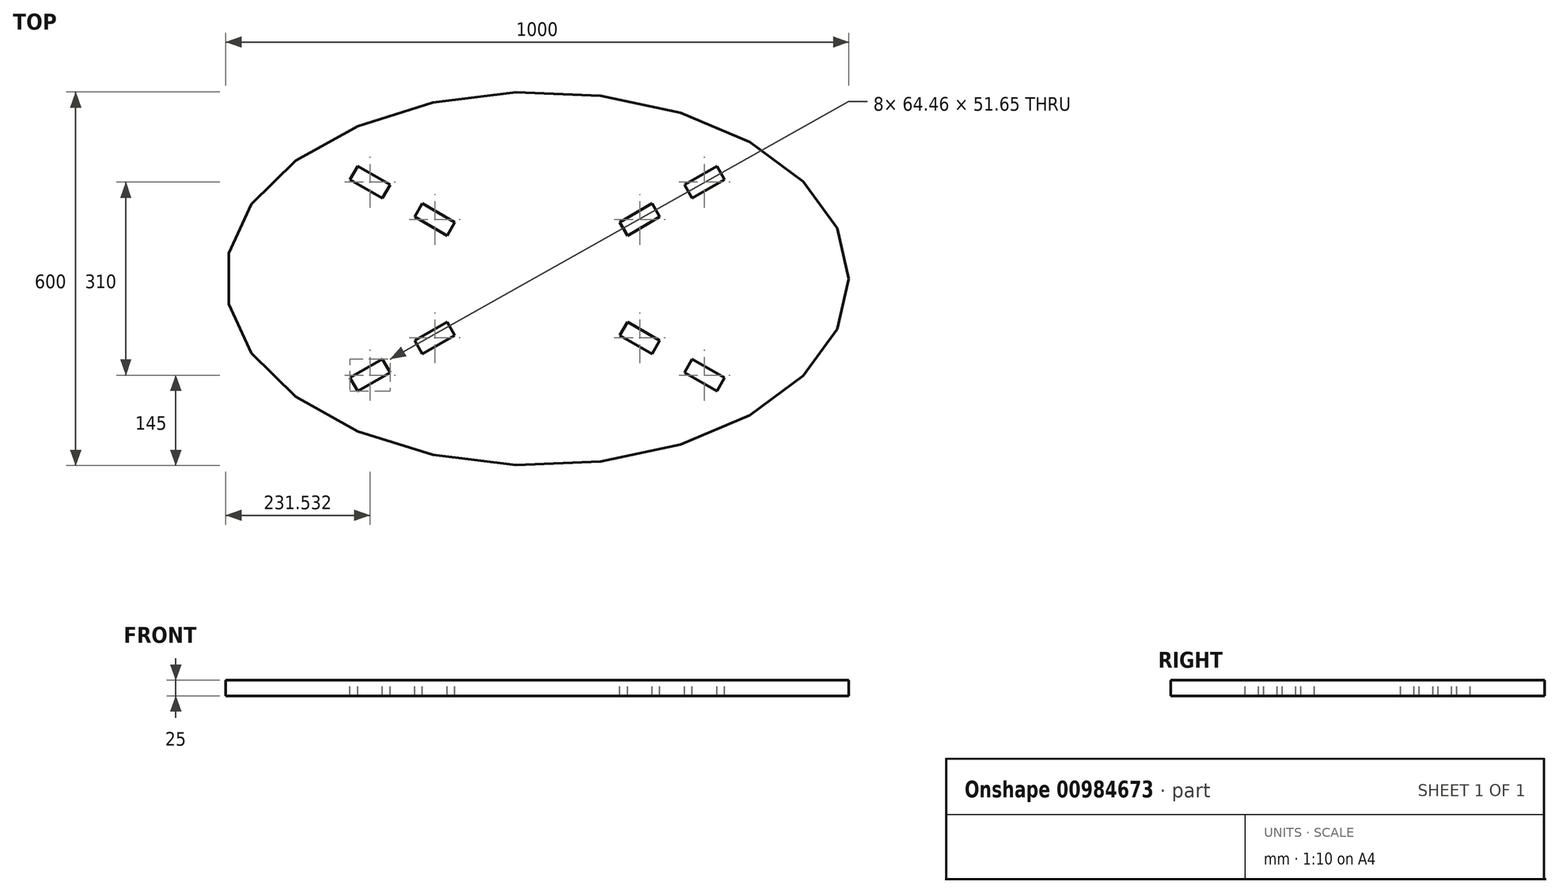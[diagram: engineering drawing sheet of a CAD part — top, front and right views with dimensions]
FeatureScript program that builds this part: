
annotation { "Feature Type Name" : "Feature", "Feature Type Description" : "" }
export const myFeature = defineFeature(function(context is Context, id is Id, definition is map)
    precondition{}
    {
        {
            var Q0;
            Q0=qCreatedBy(makeId("Top.planeOp"),FACE);
            var sketch = newSketch(context, id + "F0", { "sketchPlane" : qUnion([Q0])});
            skEllipse(sketch, "E0", {"center": v(0, 0) * mm, "majorRadius": 500 * mm, "minorRadius": 300 * mm, "majorAxis": v(1, 0)});
            skSolve(sketch);
        }
        {
            var Q0;
            Q0 = qSketchRegion(id + "F0", true);
            extrude(context, id + "F1", {"entities" : qUnion([Q0]), "depth" : 25 * mm, "offsetDistance" : 25 * mm});
        }
        {
            var Q0;
            Q0=makeQuery(id+"F1.opExtrude","CAP_FACE",FACE,{"disambiguationData":[OSD([sQuery(id+"F0.wireOp",EDGE,"E0")])],"isStart":false});
            var sketch = newSketch(context, id + "F2", { "sketchPlane" : qUnion([Q0])});
            skPoint(sketch, "E1.endSnap0", {"position": v(-500, 0) * mm});
            skLineSegment(sketch, "E2", {"start": v(-590.32, 0) * mm, "end": v(531.22, 0) * mm, "construction": true});
            skLineSegment(sketch, "E3", {"start": v(0, 416.64) * mm, "end": v(0, -392.67) * mm, "construction": true});
            skLineSegment(sketch, "E4", {"start": v(0, 0) * mm, "end": v(-427.79, 246.98) * mm, "construction": true});
            skLineSegment(sketch, "E5", {"start": v(-288.2, 180.83) * mm, "end": v(-236.24, 150.83) * mm});
            skLineSegment(sketch, "E6", {"start": v(-236.24, 150.83) * mm, "end": v(-248.74, 129.17) * mm});
            skLineSegment(sketch, "E7", {"start": v(-248.74, 129.17) * mm, "end": v(-300.7, 159.17) * mm});
            skLineSegment(sketch, "E8", {"start": v(-300.7, 159.17) * mm, "end": v(-288.2, 180.83) * mm});
            skLineSegment(sketch, "E9", {"start": v(-184.28, 120.83) * mm, "end": v(-132.31, 90.83) * mm});
            skLineSegment(sketch, "E10", {"start": v(-132.31, 90.83) * mm, "end": v(-144.81, 69.17) * mm});
            skLineSegment(sketch, "E11", {"start": v(-144.81, 69.17) * mm, "end": v(-196.78, 99.17) * mm});
            skLineSegment(sketch, "E12", {"start": v(-196.78, 99.17) * mm, "end": v(-184.28, 120.83) * mm});
            skLineSegment(sketch, "E13.MirrorCS", {"start": v(-196.78, -99.17) * mm, "end": v(-184.28, -120.83) * mm});
            skLineSegment(sketch, "E14.MirrorCS", {"start": v(-300.7, -159.17) * mm, "end": v(-288.2, -180.83) * mm});
            skLineSegment(sketch, "E15.MirrorCS", {"start": v(-184.28, -120.83) * mm, "end": v(-132.31, -90.83) * mm});
            skLineSegment(sketch, "E16.MirrorCS", {"start": v(-236.24, -150.83) * mm, "end": v(-248.74, -129.17) * mm});
            skLineSegment(sketch, "E17.MirrorCS", {"start": v(-132.31, -90.83) * mm, "end": v(-144.81, -69.17) * mm});
            skLineSegment(sketch, "E18.MirrorCS", {"start": v(-248.74, -129.17) * mm, "end": v(-300.7, -159.17) * mm});
            skLineSegment(sketch, "E19.MirrorCS", {"start": v(-288.2, -180.83) * mm, "end": v(-236.24, -150.83) * mm});
            skLineSegment(sketch, "E20.MirrorCS", {"start": v(-144.81, -69.17) * mm, "end": v(-196.78, -99.17) * mm});
            skLineSegment(sketch, "E21.MirrorCS", {"start": v(0, -416.64) * mm, "end": v(0, 392.67) * mm, "construction": true});
            skLineSegment(sketch, "E22.MirrorCS", {"start": v(132.31, -90.83) * mm, "end": v(144.81, -69.17) * mm});
            skLineSegment(sketch, "E23.MirrorCS", {"start": v(300.7, -159.17) * mm, "end": v(288.2, -180.83) * mm});
            skLineSegment(sketch, "E24.MirrorCS", {"start": v(236.24, 150.83) * mm, "end": v(248.74, 129.17) * mm});
            skLineSegment(sketch, "E25.MirrorCS", {"start": v(236.24, -150.83) * mm, "end": v(248.74, -129.17) * mm});
            skLineSegment(sketch, "E26.MirrorCS", {"start": v(196.78, 99.17) * mm, "end": v(184.28, 120.83) * mm});
            skLineSegment(sketch, "E27.MirrorCS", {"start": v(196.78, -99.17) * mm, "end": v(184.28, -120.83) * mm});
            skLineSegment(sketch, "E28.MirrorCS", {"start": v(132.31, 90.83) * mm, "end": v(144.81, 69.17) * mm});
            skLineSegment(sketch, "E29.MirrorCS", {"start": v(300.7, 159.17) * mm, "end": v(288.2, 180.83) * mm});
            skLineSegment(sketch, "E30.MirrorCS", {"start": v(184.28, 120.83) * mm, "end": v(132.31, 90.83) * mm});
            skLineSegment(sketch, "E31.MirrorCS", {"start": v(288.2, -180.83) * mm, "end": v(236.24, -150.83) * mm});
            skLineSegment(sketch, "E32.MirrorCS", {"start": v(248.74, -129.17) * mm, "end": v(300.7, -159.17) * mm});
            skLineSegment(sketch, "E33.MirrorCS", {"start": v(144.81, 69.17) * mm, "end": v(196.78, 99.17) * mm});
            skLineSegment(sketch, "E34.MirrorCS", {"start": v(144.81, -69.17) * mm, "end": v(196.78, -99.17) * mm});
            skLineSegment(sketch, "E35.MirrorCS", {"start": v(184.28, -120.83) * mm, "end": v(132.31, -90.83) * mm});
            skLineSegment(sketch, "E36.MirrorCS", {"start": v(288.2, 180.83) * mm, "end": v(236.24, 150.83) * mm});
            skLineSegment(sketch, "E37.MirrorCS", {"start": v(248.74, 129.17) * mm, "end": v(300.7, 159.17) * mm});
            skSolve(sketch);
        }
        {
            var Q0;
            Q0 = qSketchRegion(id + "F2", true);
            extrude(context, id + "F3", {"entities" : qUnion([Q0]), "operationType" : NewBodyOperationType.REMOVE, "oppositeDirection" : true, "depth" : 25 * mm, "offsetDistance" : 25 * mm});
        }
    });
